# Revit family: 879-008X99-001-DN65-600
name_source: partatom
category: Pipe Accessories
units: mm (PartAtom-declared; Revit-internal decimal feet)

## family parameters
Always vertical = Yes
Cut with Voids When Loaded = No
Part Type = Valve - Breaks Into
Round Connector Dimension = Use Diameter
Shared = No
Work Plane-Based = No

## types (14) — shared parameters
879-0065-00-14400849999 = DN65_PN10/16
879-0080-00-14400849999 = DN80_PN10/16
879-0100-00-14400849999 = DN100_PN10/16
879-0125-00-14400849999 = DN125_PN10/16
879-0150-00-14400849999 = DN150_PN10/16
879-0200-00-14400849999 = DN200_PN16
879-0250-00-14400849999 = DN250_PN16
879-0300-00-14400849999 = DN300_PN16
879-0350-00-14400849999 = DN350_PN16
879-0400-00-14400849999 = DN400_PN16
879-0450-00-14400849999 = DN450_PN16
879-0500-00-14400849999 = DN500_PN16
879-0600-00-04400849999 = DN600_PN10
879-0600-00-14400849999 = DN600_PN16
Body_wall_thickness = 10 mm  [stored 0.0328084 ft]
Description_ = AVK SURGE ANTICIP./RELIEF CONTROL VALVE
Search_Table = 879-008X99-001-DN65-600
URL product pages = https://www.avkvalves.com

## per-type parameters (varying)
- 879-0065-00-14400849999_DN65_PN10/16: Body_Collar_Dia=30 mm  [stored 0.0984252 ft]; Body_Collar_Dia_2=26 mm; Body_Flange_Dia=83 mm; Body_Flange_Dia_2=85 mm; Body_Height_1=73 mm; Body_Height_2=36 mm; Body_Height_3=58 mm; Body_Height_4=51 mm; Body_Top_Dia=13 mm; Body_Top_Dia_2=11 mm; Body_With_Dia=58 mm; Body_With_Dia_1=73 mm; Body_With_Dia_2=78 mm; Bolt_support=215 mm; Bolt_support_2=107 mm; Bolt_support_Dia=12 mm  [stored 0.0393701 ft]; Bolt_support_lenght=53 mm; Bolt_support_lenght_2=63 mm; Bottom_profile=16 mm  [stored 0.0524934 ft]; D1=59 mm; D1_Ref=80 mm; D3=93 mm; D4=74 mm; DN=65 mm; Fillet_Length=6 mm  [stored 0.019685 ft]; Flange_thickness=19 mm  [stored 0.062336 ft]; H3=453 mm; H3_ref=331 mm; ID=33 mm; L=290 mm; L_ref=136 mm; PG_Dia=50 mm; PG_Dia_2=25 mm  [stored 0.082021 ft]; PG_Ref=48 mm; PG_depth=8 mm  [stored 0.0262467 ft]; PG_height=291 mm; PG_height_1=266 mm; PG_ref=43 mm  [stored 0.141076 ft]; PR_1=35 mm  [stored 0.114829 ft]; P_lenght=22 mm  [stored 0.0721785 ft]; Pilot_Dia_1=18 mm; Pilot_Dia_2=20 mm  [stored 0.0656168 ft]; Pilot_Dia_3=12 mm  [stored 0.0393701 ft]; Pilot_Dia_4=6 mm  [stored 0.019685 ft]; Pilot_Dia_5=4 mm  [stored 0.0131234 ft]; Pilot_top_1=221 mm; Pilot_top_ref=30 mm  [stored 0.0984252 ft]; Profile1_Height=165 mm; Profile1_Length=25 mm  [stored 0.082021 ft]; Profile1_Length_2=17 mm; Profile_Dia=6 mm  [stored 0.019685 ft]; Profile_Dia_2=6 mm  [stored 0.019685 ft]; Profile_Dia_3=12 mm  [stored 0.0393701 ft]; Profile_Dia_ref=3 mm  [stored 0.00984252 ft]; Profile_height ref=41 mm; T_Height=155 mm; T_Height_2=132 mm; T_Height_Ref_1=22 mm  [stored 0.0721785 ft]; T_Height_Ref_2=26 mm; Top_Profile=129 mm; Top_Profile_Ref=134 mm; W=324 mm; W_Ref=301 mm; W_Ref_2=150 mm; W_Ref_4=321 mm; W_ref_3=324 mm
- 879-0080-00-14400849999_DN80_PN10/16: Body_Collar_Dia=32 mm; Body_Collar_Dia_2=28 mm; Body_Flange_Dia=89 mm; Body_Flange_Dia_2=91 mm; Body_Height_1=78 mm; Body_Height_2=39 mm; Body_Height_3=62 mm; Body_Height_4=54 mm; Body_Top_Dia=14 mm  [stored 0.0459318 ft]; Body_Top_Dia_2=12 mm  [stored 0.0393701 ft]; Body_With_Dia=62 mm; Body_With_Dia_1=78 mm; Body_With_Dia_2=84 mm; Bolt_support=230 mm; Bolt_support_2=115 mm; Bolt_support_Dia=12 mm  [stored 0.0393701 ft]; Bolt_support_lenght=60 mm; Bolt_support_lenght_2=70 mm; Bottom_profile=20 mm  [stored 0.0656168 ft]; D1=66 mm; D1_Ref=75 mm; D3=100 mm; D4=80 mm; DN=80 mm; Fillet_Length=6 mm  [stored 0.019685 ft]; Flange_thickness=19 mm  [stored 0.062336 ft]; H3=470 mm; H3_ref=339 mm; ID=40 mm  [stored 0.131234 ft]; L=310 mm; L_ref=146 mm; PG_Dia=50 mm; PG_Dia_2=25 mm  [stored 0.082021 ft]; PG_Ref=52 mm; PG_depth=8 mm  [stored 0.0262467 ft]; PG_height=293 mm; PG_height_1=268 mm; PG_ref=50 mm; PR_1=37 mm; P_lenght=25 mm  [stored 0.082021 ft]; Pilot_Dia_1=20 mm  [stored 0.0656168 ft]; Pilot_Dia_2=22 mm  [stored 0.0721785 ft]; Pilot_Dia_3=13 mm; Pilot_Dia_4=7 mm  [stored 0.0229659 ft]; Pilot_Dia_5=4 mm  [stored 0.0131234 ft]; Pilot_top_1=235 mm; Pilot_top_ref=31 mm  [stored 0.101706 ft]; Profile1_Height=165 mm; Profile1_Length=27 mm; Profile1_Length_2=18 mm; Profile_Dia=6 mm  [stored 0.019685 ft]; Profile_Dia_2=6 mm  [stored 0.019685 ft]; Profile_Dia_3=12 mm  [stored 0.0393701 ft]; Profile_Dia_ref=3 mm  [stored 0.00984252 ft]; Profile_height ref=41 mm; T_Height=164 mm; T_Height_2=141 mm; T_Height_Ref_1=23 mm; T_Height_Ref_2=27 mm; Top_Profile=138 mm; Top_Profile_Ref=143 mm; W=339 mm; W_Ref=314 mm; W_Ref_2=157 mm; W_Ref_4=336 mm; W_ref_3=339 mm
- 879-0100-00-14400849999_DN100_PN10/16: Body_Collar_Dia=36 mm; Body_Collar_Dia_2=31 mm  [stored 0.101706 ft]; Body_Flange_Dia=100 mm; Body_Flange_Dia_2=103 mm; Body_Height_1=88 mm; Body_Height_2=44 mm; Body_Height_3=59 mm; Body_Height_4=59 mm; Body_Top_Dia=16 mm  [stored 0.0524934 ft]; Body_Top_Dia_2=13 mm; Body_With_Dia=70 mm; Body_With_Dia_1=88 mm; Body_With_Dia_2=95 mm; Bolt_support=259 mm; Bolt_support_2=130 mm; Bolt_support_Dia=12 mm  [stored 0.0393701 ft]; Bolt_support_lenght=70 mm; Bolt_support_lenght_2=80 mm; Bottom_profile=25 mm  [stored 0.082021 ft]; D1=78 mm; D1_Ref=78 mm; D3=110 mm; D4=88 mm; DN=100 mm; Fillet_Length=6 mm  [stored 0.019685 ft]; Flange_thickness=19 mm  [stored 0.062336 ft]; H3=488 mm; H3_ref=345 mm; ID=50 mm; L=350 mm; L_ref=166 mm; PG_Dia=50 mm; PG_Dia_2=25 mm  [stored 0.082021 ft]; PG_Ref=58 mm; PG_depth=8 mm  [stored 0.0262467 ft]; PG_height=295 mm; PG_height_1=270 mm; PG_ref=60 mm; PR_1=39 mm; P_lenght=28 mm; Pilot_Dia_1=22 mm  [stored 0.0721785 ft]; Pilot_Dia_2=25 mm  [stored 0.082021 ft]; Pilot_Dia_3=15 mm  [stored 0.0492126 ft]; Pilot_Dia_4=7 mm  [stored 0.0229659 ft]; Pilot_Dia_5=5 mm  [stored 0.0164042 ft]; Pilot_top_1=248 mm; Pilot_top_ref=33 mm; Profile1_Height=165 mm; Profile1_Length=30 mm  [stored 0.0984252 ft]; Profile1_Length_2=20 mm  [stored 0.0656168 ft]; Profile_Dia=6 mm  [stored 0.019685 ft]; Profile_Dia_2=6 mm  [stored 0.019685 ft]; Profile_Dia_3=12 mm  [stored 0.0393701 ft]; Profile_Dia_ref=3 mm  [stored 0.00984252 ft]; Profile_height ref=41 mm; T_Height=172 mm; T_Height_2=147 mm; T_Height_Ref_1=25 mm  [stored 0.082021 ft]; T_Height_Ref_2=29 mm; Top_Profile=156 mm; Top_Profile_Ref=161 mm; W=351 mm; W_Ref=323 mm; W_Ref_2=161 mm; W_Ref_4=348 mm; W_ref_3=351 mm
- 879-0125-00-14400849999_DN125_PN10/16: Body_Collar_Dia=42 mm; Body_Collar_Dia_2=36 mm; Body_Flange_Dia=114 mm; Body_Flange_Dia_2=118 mm; Body_Height_1=100 mm; Body_Height_2=50 mm; Body_Height_3=65 mm; Body_Height_4=65 mm; Body_Top_Dia=18 mm; Body_Top_Dia_2=15 mm  [stored 0.0492126 ft]; Body_With_Dia=80 mm; Body_With_Dia_1=100 mm; Body_With_Dia_2=108 mm; Bolt_support=296 mm; Bolt_support_2=148 mm; Bolt_support_Dia=12 mm  [stored 0.0393701 ft]; Bolt_support_lenght=83 mm; Bolt_support_lenght_2=93 mm; Bottom_profile=31 mm  [stored 0.101706 ft]; D1=92 mm; D1_Ref=92 mm; D3=125 mm; D4=100 mm; DN=125 mm; Fillet_Length=6 mm  [stored 0.019685 ft]; Flange_thickness=19 mm  [stored 0.062336 ft]; H3=506 mm; H3_ref=347 mm; ID=63 mm; L=400 mm; L_ref=191 mm; PG_Dia=50 mm; PG_Dia_2=25 mm  [stored 0.082021 ft]; PG_Ref=67 mm; PG_depth=8 mm  [stored 0.0262467 ft]; PG_height=296 mm; PG_height_1=271 mm; PG_ref=73 mm; PR_1=40 mm  [stored 0.131234 ft]; P_lenght=35 mm  [stored 0.114829 ft]; Pilot_Dia_1=28 mm; Pilot_Dia_2=32 mm; Pilot_Dia_3=18 mm; Pilot_Dia_4=9 mm  [stored 0.0295276 ft]; Pilot_Dia_5=6 mm  [stored 0.019685 ft]; Pilot_top_1=274 mm; Pilot_top_ref=34 mm; Profile1_Height=165 mm; Profile1_Length=34 mm; Profile1_Length_2=23 mm; Profile_Dia=6 mm  [stored 0.019685 ft]; Profile_Dia_2=6 mm  [stored 0.019685 ft]; Profile_Dia_3=12 mm  [stored 0.0393701 ft]; Profile_Dia_ref=3 mm  [stored 0.00984252 ft]; Profile_height ref=41 mm; T_Height=175 mm; T_Height_2=150 mm; T_Height_Ref_1=25 mm  [stored 0.082021 ft]; T_Height_Ref_2=29 mm; Top_Profile=178 mm; Top_Profile_Ref=183 mm; W=375 mm; W_Ref=340 mm; W_Ref_2=170 mm; W_Ref_4=372 mm; W_ref_3=375 mm
- 879-0150-00-14400849999_DN150_PN10/16: Body_Collar_Dia=50 mm; Body_Collar_Dia_2=43 mm  [stored 0.141076 ft]; Body_Flange_Dia=137 mm; Body_Flange_Dia_2=141 mm; Body_Height_1=120 mm; Body_Height_2=60 mm; Body_Height_3=60 mm; Body_Height_4=75 mm; Body_Top_Dia=22 mm  [stored 0.0721785 ft]; Body_Top_Dia_2=18 mm; Body_With_Dia=96 mm; Body_With_Dia_1=120 mm; Body_With_Dia_2=130 mm; Bolt_support=356 mm; Bolt_support_2=178 mm; Bolt_support_Dia=16 mm  [stored 0.0524934 ft]; Bolt_support_lenght=95 mm; Bolt_support_lenght_2=105 mm; Bottom_profile=38 mm; D1=106 mm; D1_Ref=106 mm; D3=143 mm; D4=114 mm; DN=150 mm; Fillet_Length=8 mm  [stored 0.0262467 ft]; Flange_thickness=19 mm  [stored 0.062336 ft]; H3=509 mm; H3_ref=342 mm; ID=75 mm; L=480 mm; L_ref=231 mm; PG_Dia=80 mm; PG_Dia_2=40 mm  [stored 0.131234 ft]; PG_Ref=80 mm; PG_depth=11 mm; PG_height=347 mm; PG_height_1=307 mm; PG_ref=85 mm; PR_1=29 mm; P_lenght=39 mm; Pilot_Dia_1=31 mm  [stored 0.101706 ft]; Pilot_Dia_2=36 mm; Pilot_Dia_3=21 mm  [stored 0.0688976 ft]; Pilot_Dia_4=10 mm  [stored 0.0328084 ft]; Pilot_Dia_5=7 mm  [stored 0.0229659 ft]; Pilot_top_1=290 mm; Pilot_top_ref=25 mm  [stored 0.082021 ft]; Profile1_Height=195 mm; Profile1_Length=39 mm; Profile1_Length_2=26 mm; Profile_Dia=8 mm  [stored 0.0262467 ft]; Profile_Dia_2=8 mm  [stored 0.0262467 ft]; Profile_Dia_3=16 mm  [stored 0.0524934 ft]; Profile_Dia_ref=4 mm  [stored 0.0131234 ft]; Profile_height ref=43 mm  [stored 0.141076 ft]; T_Height=129 mm; T_Height_2=110 mm; T_Height_Ref_1=18 mm; T_Height_Ref_2=21 mm  [stored 0.0688976 ft]; Top_Profile=213 mm; Top_Profile_Ref=218 mm; W=405 mm; W_Ref=365 mm; W_Ref_2=183 mm; W_Ref_4=401 mm; W_ref_3=405 mm
- 879-0200-00-14400849999_DN200_PN16: Body_Collar_Dia=63 mm; Body_Collar_Dia_2=54 mm; Body_Flange_Dia=171 mm; Body_Flange_Dia_2=176 mm; Body_Height_1=150 mm; Body_Height_2=75 mm; Body_Height_3=75 mm; Body_Height_4=90 mm; Body_Top_Dia=27 mm; Body_Top_Dia_2=22 mm  [stored 0.0721785 ft]; Body_With_Dia=120 mm; Body_With_Dia_1=150 mm; Body_With_Dia_2=162 mm; Bolt_support=444 mm; Bolt_support_2=222 mm; Bolt_support_Dia=20 mm  [stored 0.0656168 ft]; Bolt_support_lenght=120 mm; Bolt_support_lenght_2=130 mm; Bottom_profile=50 mm; D1=133 mm; D1_Ref=133 mm; D3=170 mm; D4=136 mm; DN=200 mm; Fillet_Length=10 mm  [stored 0.0328084 ft]; Flange_thickness=20 mm  [stored 0.0656168 ft]; H3=605 mm; H3_ref=406 mm; ID=100 mm; L=600 mm; L_ref=290 mm; PG_Dia=80 mm; PG_Dia_2=40 mm  [stored 0.131234 ft]; PG_Ref=100 mm; PG_depth=14 mm  [stored 0.0459318 ft]; PG_height=397 mm; PG_height_1=357 mm; PG_ref=110 mm; PR_1=34 mm; P_lenght=49 mm; Pilot_Dia_1=39 mm; Pilot_Dia_2=44 mm; Pilot_Dia_3=26 mm; Pilot_Dia_4=13 mm; Pilot_Dia_5=9 mm  [stored 0.0295276 ft]; Pilot_top_1=354 mm; Pilot_top_ref=29 mm; Profile1_Height=238 mm; Profile1_Length=46 mm; Profile1_Length_2=31 mm  [stored 0.101706 ft]; Profile_Dia=10 mm  [stored 0.0328084 ft]; Profile_Dia_2=10 mm  [stored 0.0328084 ft]; Profile_Dia_3=20 mm  [stored 0.0656168 ft]; Profile_Dia_ref=5 mm  [stored 0.0164042 ft]; Profile_height ref=45 mm; T_Height=152 mm; T_Height_2=130 mm; T_Height_Ref_1=22 mm  [stored 0.0721785 ft]; T_Height_Ref_2=25 mm  [stored 0.082021 ft]; Top_Profile=267 mm; Top_Profile_Ref=272 mm; W=466 mm; W_Ref=417 mm; W_Ref_2=208 mm; W_Ref_4=461 mm; W_ref_3=466 mm
- 879-0250-00-14400849999_DN250_PN16: Body_Collar_Dia=76 mm; Body_Collar_Dia_2=65 mm; Body_Flange_Dia=209 mm; Body_Flange_Dia_2=215 mm; Body_Height_1=183 mm; Body_Height_2=91 mm; Body_Height_3=81 mm; Body_Height_4=106 mm; Body_Top_Dia=33 mm; Body_Top_Dia_2=27 mm; Body_With_Dia=146 mm; Body_With_Dia_1=183 mm; Body_With_Dia_2=197 mm; Bolt_support=541 mm; Bolt_support_2=270 mm; Bolt_support_Dia=20 mm  [stored 0.0656168 ft]; Bolt_support_lenght=145 mm; Bolt_support_lenght_2=155 mm; Bottom_profile=63 mm; D1=160 mm; D1_Ref=160 mm; D3=203 mm; D4=162 mm; DN=250 mm; Fillet_Length=10 mm  [stored 0.0328084 ft]; Flange_thickness=22 mm  [stored 0.0721785 ft]; H3=716 mm; H3_ref=476 mm; ID=125 mm; L=730 mm; L_ref=354 mm; PG_Dia=80 mm; PG_Dia_2=40 mm  [stored 0.131234 ft]; PG_Ref=122 mm; PG_depth=14 mm  [stored 0.0459318 ft]; PG_height=444 mm; PG_height_1=404 mm; PG_ref=135 mm; PR_1=44 mm; P_lenght=58 mm; Pilot_Dia_1=46 mm; Pilot_Dia_2=53 mm; Pilot_Dia_3=31 mm  [stored 0.101706 ft]; Pilot_Dia_4=15 mm  [stored 0.0492126 ft]; Pilot_Dia_5=10 mm  [stored 0.0328084 ft]; Pilot_top_1=417 mm; Pilot_top_ref=37 mm; Profile1_Height=275 mm; Profile1_Length=55 mm; Profile1_Length_2=36 mm; Profile_Dia=10 mm  [stored 0.0328084 ft]; Profile_Dia_2=10 mm  [stored 0.0328084 ft]; Profile_Dia_3=20 mm  [stored 0.0656168 ft]; Profile_Dia_ref=5 mm  [stored 0.0164042 ft]; Profile_height ref=45 mm; T_Height=194 mm; T_Height_2=166 mm; T_Height_Ref_1=28 mm; T_Height_Ref_2=32 mm; Top_Profile=324 mm; Top_Profile_Ref=329 mm; W=587 mm; W_Ref=529 mm; W_Ref_2=265 mm; W_Ref_4=582 mm; W_ref_3=587 mm
- 879-0300-00-14400849999_DN300_PN16: Body_Collar_Dia=89 mm; Body_Collar_Dia_2=76 mm; Body_Flange_Dia=243 mm; Body_Flange_Dia_2=250 mm; Body_Height_1=213 mm; Body_Height_2=106 mm; Body_Height_3=95 mm; Body_Height_4=121 mm; Body_Top_Dia=38 mm; Body_Top_Dia_2=32 mm; Body_With_Dia=170 mm; Body_With_Dia_1=213 mm; Body_With_Dia_2=230 mm; Bolt_support=630 mm; Bolt_support_2=315 mm; Bolt_support_Dia=20 mm  [stored 0.0656168 ft]; Bolt_support_lenght=170 mm; Bolt_support_lenght_2=180 mm; Bottom_profile=75 mm; D1=185 mm; D1_Ref=185 mm; D3=230 mm; D4=184 mm; DN=300 mm; Fillet_Length=10 mm  [stored 0.0328084 ft]; Flange_thickness=25 mm  [stored 0.082021 ft]; H3=789 mm; H3_ref=523 mm; ID=150 mm; L=850 mm; L_ref=413 mm; PG_Dia=90 mm; PG_Dia_2=45 mm; PG_Ref=142 mm; PG_depth=14 mm  [stored 0.0459318 ft]; PG_height=503 mm; PG_height_1=458 mm; PG_ref=160 mm; PR_1=43 mm  [stored 0.141076 ft]; P_lenght=66 mm; Pilot_Dia_1=53 mm; Pilot_Dia_2=60 mm; Pilot_Dia_3=35 mm  [stored 0.114829 ft]; Pilot_Dia_4=18 mm; Pilot_Dia_5=12 mm  [stored 0.0393701 ft]; Pilot_top_1=475 mm; Pilot_top_ref=36 mm; Profile1_Height=325 mm; Profile1_Length=62 mm; Profile1_Length_2=41 mm; Profile_Dia=10 mm  [stored 0.0328084 ft]; Profile_Dia_2=10 mm  [stored 0.0328084 ft]; Profile_Dia_3=20 mm  [stored 0.0656168 ft]; Profile_Dia_ref=5 mm  [stored 0.0164042 ft]; Profile_height ref=45 mm; T_Height=189 mm; T_Height_2=162 mm; T_Height_Ref_1=27 mm; T_Height_Ref_2=32 mm; Top_Profile=378 mm; Top_Profile_Ref=383 mm; W=629 mm; W_Ref=564 mm; W_Ref_2=282 mm; W_Ref_4=624 mm; W_ref_3=629 mm
- 879-0350-00-14400849999_DN350_PN16: Body_Collar_Dia=102 mm; Body_Collar_Dia_2=88 mm; Body_Flange_Dia=280 mm; Body_Flange_Dia_2=288 mm; Body_Height_1=245 mm; Body_Height_2=123 mm; Body_Height_3=98 mm; Body_Height_4=138 mm; Body_Top_Dia=44 mm; Body_Top_Dia_2=37 mm; Body_With_Dia=196 mm; Body_With_Dia_1=245 mm; Body_With_Dia_2=265 mm; Bolt_support=726 mm; Bolt_support_2=363 mm; Bolt_support_Dia=30 mm  [stored 0.0984252 ft]; Bolt_support_lenght=195 mm; Bolt_support_lenght_2=205 mm; Bottom_profile=88 mm; D1=215 mm; D1_Ref=215 mm; D3=260 mm; D4=208 mm; DN=350 mm; Fillet_Length=15 mm  [stored 0.0492126 ft]; Flange_thickness=27 mm; H3=875 mm; H3_ref=577 mm; ID=175 mm; L=980 mm; L_ref=477 mm; PG_Dia=110 mm; PG_Dia_2=55 mm; PG_Ref=163 mm; PG_depth=21 mm  [stored 0.0688976 ft]; PG_height=570 mm; PG_height_1=515 mm; PG_ref=185 mm; PR_1=45 mm; P_lenght=77 mm; Pilot_Dia_1=61 mm; Pilot_Dia_2=70 mm; Pilot_Dia_3=40 mm  [stored 0.131234 ft]; Pilot_Dia_4=20 mm  [stored 0.0656168 ft]; Pilot_Dia_5=13 mm; Pilot_top_1=529 mm; Pilot_top_ref=38 mm; Profile1_Height=365 mm; Profile1_Length=70 mm; Profile1_Length_2=47 mm; Profile_Dia=15 mm  [stored 0.0492126 ft]; Profile_Dia_2=15 mm  [stored 0.0492126 ft]; Profile_Dia_3=30 mm  [stored 0.0984252 ft]; Profile_Dia_ref=8 mm  [stored 0.0262467 ft]; Profile_height ref=50 mm; T_Height=200 mm; T_Height_2=171 mm; T_Height_Ref_1=29 mm; T_Height_Ref_2=33 mm; Top_Profile=436 mm; Top_Profile_Ref=441 mm; W=690 mm; W_Ref=613 mm; W_Ref_2=306 mm; W_Ref_4=683 mm; W_ref_3=690 mm
- 879-0400-00-14400849999_DN400_PN16: Body_Collar_Dia=115 mm; Body_Collar_Dia_2=99 mm; Body_Flange_Dia=314 mm; Body_Flange_Dia_2=324 mm; Body_Height_1=275 mm; Body_Height_2=138 mm; Body_Height_3=110 mm; Body_Height_4=153 mm; Body_Top_Dia=49 mm; Body_Top_Dia_2=41 mm; Body_With_Dia=220 mm; Body_With_Dia_1=275 mm; Body_With_Dia_2=297 mm; Bolt_support=815 mm; Bolt_support_2=407 mm; Bolt_support_Dia=40 mm  [stored 0.131234 ft]; Bolt_support_lenght=220 mm; Bolt_support_lenght_2=230 mm; Bottom_profile=100 mm; D1=240 mm; D1_Ref=240 mm; D3=290 mm; D4=232 mm; DN=400 mm; Fillet_Length=20 mm  [stored 0.0656168 ft]; Flange_thickness=28 mm; H3=996 mm; H3_ref=657 mm; ID=200 mm; L=1100 mm; L_ref=536 mm; PG_Dia=110 mm; PG_Dia_2=55 mm; PG_Ref=183 mm; PG_depth=28 mm; PG_height=618 mm; PG_height_1=563 mm; PG_ref=210 mm; PR_1=58 mm; P_lenght=87 mm; Pilot_Dia_1=69 mm; Pilot_Dia_2=79 mm; Pilot_Dia_3=46 mm; Pilot_Dia_4=23 mm; Pilot_Dia_5=15 mm  [stored 0.0492126 ft]; Pilot_top_1=597 mm; Pilot_top_ref=49 mm; Profile1_Height=395 mm; Profile1_Length=78 mm; Profile1_Length_2=52 mm; Profile_Dia=20 mm  [stored 0.0656168 ft]; Profile_Dia_2=20 mm  [stored 0.0656168 ft]; Profile_Dia_3=40 mm  [stored 0.131234 ft]; Profile_Dia_ref=10 mm  [stored 0.0328084 ft]; Profile_height ref=55 mm; T_Height=256 mm; T_Height_2=219 mm; T_Height_Ref_1=37 mm; T_Height_Ref_2=43 mm  [stored 0.141076 ft]; Top_Profile=489 mm; Top_Profile_Ref=494 mm; W=750 mm; W_Ref=661 mm; W_Ref_2=330 mm; W_Ref_4=740 mm; W_ref_3=750 mm
- 879-0450-00-14400849999_DN450_PN16: Body_Collar_Dia=125 mm; Body_Collar_Dia_2=108 mm; Body_Flange_Dia=343 mm; Body_Flange_Dia_2=353 mm; Body_Height_1=300 mm; Body_Height_2=150 mm; Body_Height_3=120 mm; Body_Height_4=165 mm; Body_Top_Dia=54 mm; Body_Top_Dia_2=45 mm; Body_With_Dia=240 mm; Body_With_Dia_1=300 mm; Body_With_Dia_2=324 mm; Bolt_support=889 mm; Bolt_support_2=444 mm; Bolt_support_Dia=40 mm  [stored 0.131234 ft]; Bolt_support_lenght=245 mm; Bolt_support_lenght_2=255 mm; Bottom_profile=113 mm; D1=274 mm; D1_Ref=265 mm; D3=320 mm; D4=256 mm; DN=450 mm; Fillet_Length=20 mm  [stored 0.0656168 ft]; Flange_thickness=30 mm  [stored 0.0984252 ft]; H3=1060 mm; H3_ref=694 mm; ID=225 mm; L=1200 mm; L_ref=585 mm; PG_Dia=130 mm; PG_Dia_2=65 mm; PG_Ref=200 mm; PG_depth=28 mm; PG_height=684 mm; PG_height_1=619 mm; PG_ref=235 mm; PR_1=54 mm; P_lenght=96 mm; Pilot_Dia_1=76 mm; Pilot_Dia_2=87 mm; Pilot_Dia_3=50 mm; Pilot_Dia_4=25 mm  [stored 0.082021 ft]; Pilot_Dia_5=17 mm; Pilot_top_1=641 mm; Pilot_top_ref=46 mm; Profile1_Height=445 mm; Profile1_Length=86 mm; Profile1_Length_2=58 mm; Profile_Dia=20 mm  [stored 0.0656168 ft]; Profile_Dia_2=20 mm  [stored 0.0656168 ft]; Profile_Dia_3=40 mm  [stored 0.131234 ft]; Profile_Dia_ref=10 mm  [stored 0.0328084 ft]; Profile_height ref=55 mm; T_Height=240 mm; T_Height_2=206 mm; T_Height_Ref_1=34 mm; T_Height_Ref_2=40 mm  [stored 0.131234 ft]; Top_Profile=533 mm; Top_Profile_Ref=538 mm; W=810 mm; W_Ref=713 mm; W_Ref_2=357 mm; W_Ref_4=800 mm; W_ref_3=810 mm
- 879-0500-00-14400849999_DN500_PN16: Body_Collar_Dia=130 mm; Body_Collar_Dia_2=112 mm; Body_Flange_Dia=357 mm; Body_Flange_Dia_2=368 mm; Body_Height_1=313 mm; Body_Height_2=156 mm; Body_Height_3=125 mm; Body_Height_4=171 mm; Body_Top_Dia=56 mm; Body_Top_Dia_2=47 mm; Body_With_Dia=250 mm; Body_With_Dia_1=313 mm; Body_With_Dia_2=338 mm; Bolt_support=926 mm; Bolt_support_2=463 mm; Bolt_support_Dia=50 mm; Bolt_support_lenght=270 mm; Bolt_support_lenght_2=280 mm; Bottom_profile=125 mm; D1=305 mm; D1_Ref=291 mm; D3=358 mm; D4=286 mm; DN=500 mm; Fillet_Length=25 mm  [stored 0.082021 ft]; Flange_thickness=32 mm; H3=1245 mm; H3_ref=815 mm; ID=250 mm; L=1250 mm; L_ref=609 mm; PG_Dia=130 mm; PG_Dia_2=65 mm; PG_Ref=208 mm; PG_depth=35 mm  [stored 0.114829 ft]; PG_height=725 mm; PG_height_1=660 mm; PG_ref=260 mm; PR_1=85 mm; P_lenght=105 mm; Pilot_Dia_1=83 mm; Pilot_Dia_2=95 mm; Pilot_Dia_3=55 mm; Pilot_Dia_4=28 mm; Pilot_Dia_5=18 mm; Pilot_top_1=691 mm; Pilot_top_ref=72 mm; Profile1_Height=450 mm; Profile1_Length=97 mm; Profile1_Length_2=64 mm; Profile_Dia=25 mm  [stored 0.082021 ft]; Profile_Dia_2=25 mm  [stored 0.082021 ft]; Profile_Dia_3=50 mm; Profile_Dia_ref=13 mm; Profile_height ref=60 mm; T_Height=378 mm; T_Height_2=324 mm; T_Height_Ref_1=54 mm; T_Height_Ref_2=63 mm; Top_Profile=556 mm; Top_Profile_Ref=561 mm; W=885 mm; W_Ref=777 mm; W_Ref_2=389 mm; W_Ref_4=873 mm; W_ref_3=885 mm
- 879-0600-00-04400849999_DN600_PN10: Body_Collar_Dia=151 mm; Body_Collar_Dia_2=130 mm; Body_Flange_Dia=414 mm; Body_Flange_Dia_2=426 mm; Body_Height_1=363 mm; Body_Height_2=181 mm; Body_Height_3=145 mm; Body_Height_4=196 mm; Body_Top_Dia=65 mm; Body_Top_Dia_2=54 mm; Body_With_Dia=290 mm; Body_With_Dia_1=363 mm; Body_With_Dia_2=392 mm; Bolt_support=1074 mm; Bolt_support_2=537 mm; Bolt_support_Dia=60 mm; Bolt_support_lenght=320 mm; Bolt_support_lenght_2=330 mm; Bottom_profile=150 mm; D1=341 mm; D1_Ref=341 mm; D3=390 mm; D4=312 mm; DN=600 mm; Fillet_Length=30 mm  [stored 0.0984252 ft]; Flange_thickness=36 mm; H3=1355 mm; H3_ref=893 mm; ID=300 mm; L=1450 mm; L_ref=707 mm; PG_Dia=150 mm; PG_Dia_2=75 mm; PG_Ref=242 mm; PG_depth=42 mm; PG_height=825 mm; PG_height_1=750 mm; PG_ref=310 mm; PR_1=85 mm; P_lenght=124 mm; Pilot_Dia_1=98 mm; Pilot_Dia_2=113 mm; Pilot_Dia_3=65 mm; Pilot_Dia_4=33 mm; Pilot_Dia_5=22 mm  [stored 0.0721785 ft]; Pilot_top_1=786 mm; Pilot_top_ref=72 mm; Profile1_Height=525 mm; Profile1_Length=105 mm; Profile1_Length_2=70 mm; Profile_Dia=30 mm  [stored 0.0984252 ft]; Profile_Dia_2=30 mm  [stored 0.0984252 ft]; Profile_Dia_3=60 mm; Profile_Dia_ref=15 mm  [stored 0.0492126 ft]; Profile_height ref=65 mm; T_Height=375 mm; T_Height_2=321 mm; T_Height_Ref_1=54 mm; T_Height_Ref_2=63 mm; Top_Profile=644 mm; Top_Profile_Ref=649 mm; W=1010 mm; W_Ref=882 mm; W_Ref_2=441 mm; W_Ref_4=995 mm; W_ref_3=1010 mm
- 879-0600-00-14400849999_DN600_PN16: Body_Collar_Dia=151 mm; Body_Collar_Dia_2=130 mm; Body_Flange_Dia=414 mm; Body_Flange_Dia_2=426 mm; Body_Height_1=363 mm; Body_Height_2=181 mm; Body_Height_3=145 mm; Body_Height_4=196 mm; Body_Top_Dia=65 mm; Body_Top_Dia_2=54 mm; Body_With_Dia=290 mm; Body_With_Dia_1=363 mm; Body_With_Dia_2=392 mm; Bolt_support=1074 mm; Bolt_support_2=537 mm; Bolt_support_Dia=60 mm; Bolt_support_lenght=320 mm; Bolt_support_lenght_2=330 mm; Bottom_profile=150 mm; D1=360 mm; D1_Ref=370 mm; D3=420 mm; D4=336 mm; DN=600 mm; Fillet_Length=30 mm  [stored 0.0984252 ft]; Flange_thickness=37 mm; H3=1355 mm; H3_ref=871 mm; ID=300 mm; L=1450 mm; L_ref=707 mm; PG_Dia=150 mm; PG_Dia_2=75 mm; PG_Ref=242 mm; PG_depth=42 mm; PG_height=826 mm; PG_height_1=751 mm; PG_ref=310 mm; PR_1=76 mm; P_lenght=114 mm; Pilot_Dia_1=90 mm; Pilot_Dia_2=104 mm; Pilot_Dia_3=60 mm; Pilot_Dia_4=30 mm  [stored 0.0984252 ft]; Pilot_Dia_5=20 mm  [stored 0.0656168 ft]; Pilot_top_1=778 mm; Pilot_top_ref=64 mm; Profile1_Height=535 mm; Profile1_Length=114 mm; Profile1_Length_2=76 mm; Profile_Dia=30 mm  [stored 0.0984252 ft]; Profile_Dia_2=30 mm  [stored 0.0984252 ft]; Profile_Dia_3=60 mm; Profile_Dia_ref=15 mm  [stored 0.0492126 ft]; Profile_height ref=65 mm; T_Height=335 mm; T_Height_2=287 mm; T_Height_Ref_1=48 mm; T_Height_Ref_2=56 mm; Top_Profile=644 mm; Top_Profile_Ref=649 mm; W=1010 mm; W_Ref=892 mm; W_Ref_2=446 mm; W_Ref_4=995 mm; W_ref_3=1010 mm

note: [stored X ft] marks values corroborated as IEEE doubles in the binary element streams (Revit-internal decimal feet)

## geometry (parser evidence)
native form markers: Sweep x4
no freeform markers — native parametric forms only
